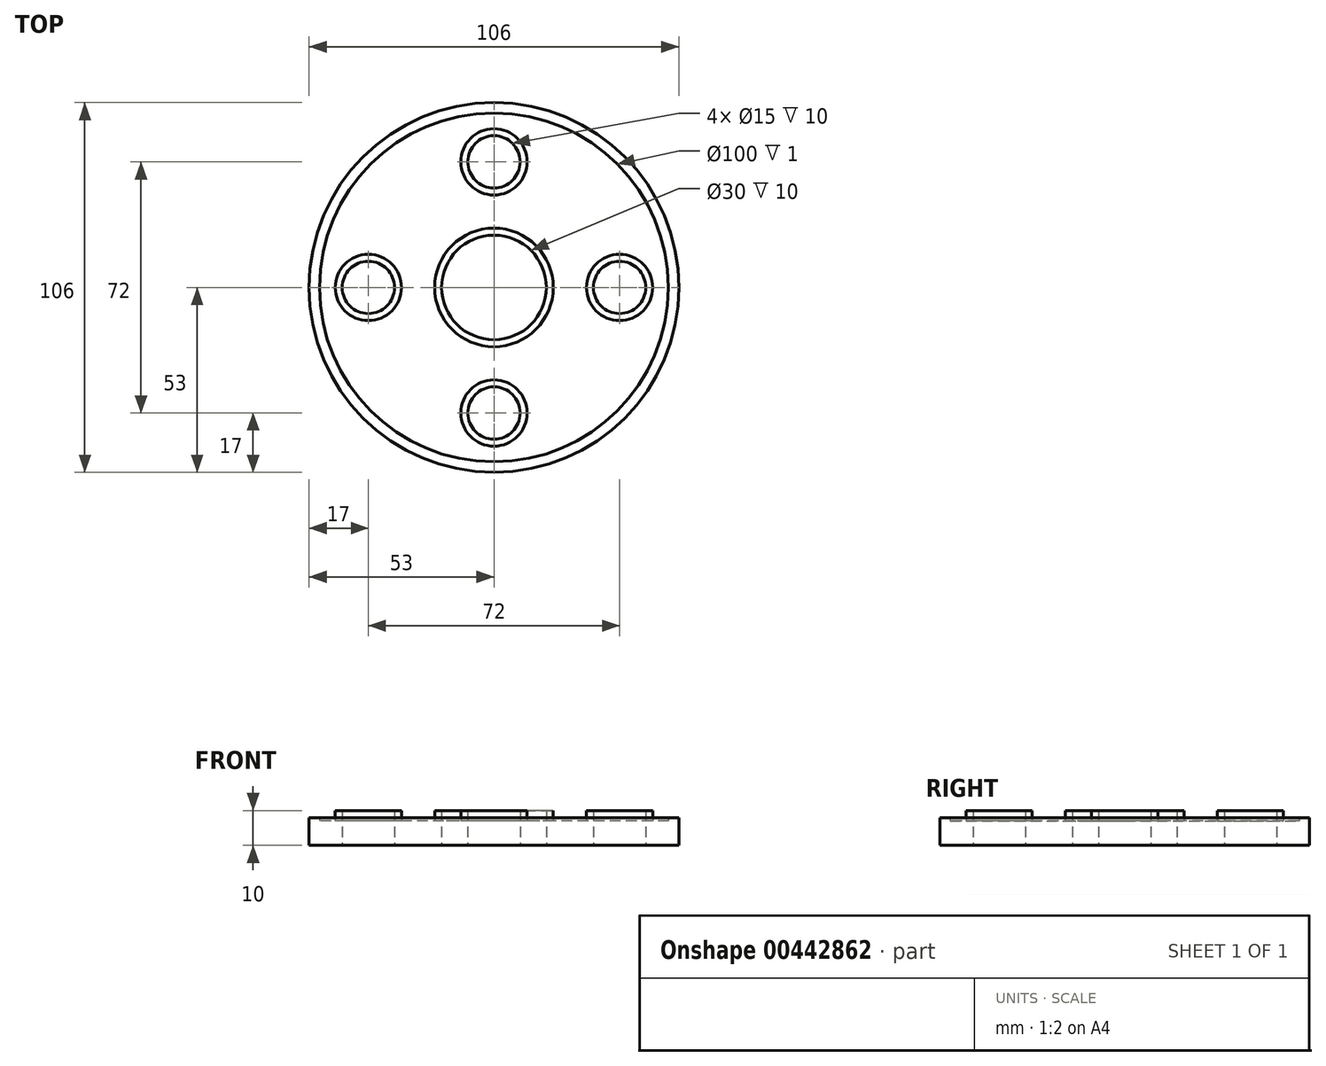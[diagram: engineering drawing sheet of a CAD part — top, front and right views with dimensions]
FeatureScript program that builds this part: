
annotation { "Feature Type Name" : "Feature", "Feature Type Description" : "" }
export const myFeature = defineFeature(function(context is Context, id is Id, definition is map)
    precondition{}
    {
        {
            var Q0;
            Q0=qCreatedBy(makeId("Top.planeOp"),FACE);
            var sketch = newSketch(context, id + "F0", { "sketchPlane" : qUnion([Q0])});
            skCircle(sketch, "E0", {"center": v(0, 0) * mm, "radius": 53 * mm});
            skCircle(sketch, "E1", {"center": v(0, 0) * mm, "radius": 50 * mm});
            skCircle(sketch, "E2", {"center": v(-36, 0) * mm, "radius": 7.5 * mm});
            skCircle(sketch, "E3", {"center": v(-36, 0) * mm, "radius": 9.5 * mm});
            skCircle(sketch, "E4", {"center": v(0, -36) * mm, "radius": 9.5 * mm});
            skCircle(sketch, "E5", {"center": v(0, -36) * mm, "radius": 7.5 * mm});
            skCircle(sketch, "E6", {"center": v(36, 0) * mm, "radius": 9.5 * mm});
            skCircle(sketch, "E7", {"center": v(36, 0) * mm, "radius": 7.5 * mm});
            skCircle(sketch, "E8", {"center": v(0, 36) * mm, "radius": 9.5 * mm});
            skCircle(sketch, "E9", {"center": v(0, 36) * mm, "radius": 7.5 * mm});
            skCircle(sketch, "E10", {"center": v(0, 0) * mm, "radius": 15 * mm});
            skCircle(sketch, "E11", {"center": v(0, 0) * mm, "radius": 17 * mm});
            skSolve(sketch);
        }
        {
            var Q0;
            Q0=makeQuery(id+"F0.imprint","IMPRINT",FACE,{"disambiguationData":[TD([[makeQuery(id+"F0.imprint","IMPRINT",EDGE,{"derivedFrom":sQuery(id+"F0.wireOp",EDGE,"E0")}),1.0]])]});
            extrude(context, id + "F1", {"entities" : qUnion([Q0]), "depth" : 7 * mm});
        }
        {
            var Q0;
            Q0=makeQuery(id+"F1.opExtrude","CAP_FACE",FACE,{"disambiguationData":[OSD([sQuery(id+"F0.wireOp",EDGE,"E0"),sQuery(id+"F0.wireOp",EDGE,"E1")])],"isStart":false});
            var Q1;
            Q1 = qSketchRegion(id + "F0", true);
            extrude(context, id + "F2", {"entities" : qUnion([Q0, Q1]), "operationType" : NewBodyOperationType.ADD, "depth" : 1 * mm});
        }
        {
            var Q0;
            Q0=makeQuery(id+"F0.imprint","IMPRINT",FACE,{"disambiguationData":[TD([[makeQuery(id+"F0.imprint","IMPRINT",EDGE,{"derivedFrom":sQuery(id+"F0.wireOp",EDGE,"E1")}),1.0]])]});
            extrude(context, id + "F3", {"entities" : qUnion([Q0]), "operationType" : NewBodyOperationType.ADD, "depth" : 7 * mm});
        }
        {
            var Q0;
            Q0=qCreatedBy(makeId("Top.planeOp"),FACE);
            var sketch = newSketch(context, id + "F4", { "sketchPlane" : qUnion([Q0])});
            skSolve(sketch);
        }
        {
            var Q0;
            Q0 = qSketchRegion(id + "F4", true);
            var Q1;
            Q1=makeQuery(id+"F0.imprint","IMPRINT",FACE,{"disambiguationData":[TD([[makeQuery(id+"F0.imprint","IMPRINT",EDGE,{"derivedFrom":sQuery(id+"F0.wireOp",EDGE,"E2")}),-1.0]])]});
            var Q2;
            Q2=makeQuery(id+"F0.imprint","IMPRINT",FACE,{"disambiguationData":[TD([[makeQuery(id+"F0.imprint","IMPRINT",EDGE,{"derivedFrom":sQuery(id+"F0.wireOp",EDGE,"E4")}),1.0]])]});
            var Q3;
            Q3=makeQuery(id+"F0.imprint","IMPRINT",FACE,{"disambiguationData":[TD([[makeQuery(id+"F0.imprint","IMPRINT",EDGE,{"derivedFrom":sQuery(id+"F0.wireOp",EDGE,"E6")}),1.0]])]});
            var Q4;
            Q4=makeQuery(id+"F0.imprint","IMPRINT",FACE,{"disambiguationData":[TD([[makeQuery(id+"F0.imprint","IMPRINT",EDGE,{"derivedFrom":sQuery(id+"F0.wireOp",EDGE,"E8")}),1.0]])]});
            var Q5;
            Q5=makeQuery(id+"F0.imprint","IMPRINT",FACE,{"disambiguationData":[TD([[makeQuery(id+"F0.imprint","IMPRINT",EDGE,{"derivedFrom":sQuery(id+"F0.wireOp",EDGE,"E10")}),-1.0]])]});
            extrude(context, id + "F5", {"entities" : qUnion([Q0, Q1, Q2, Q3, Q4, Q5]), "operationType" : NewBodyOperationType.ADD, "depth" : 10 * mm});
        }
    });
